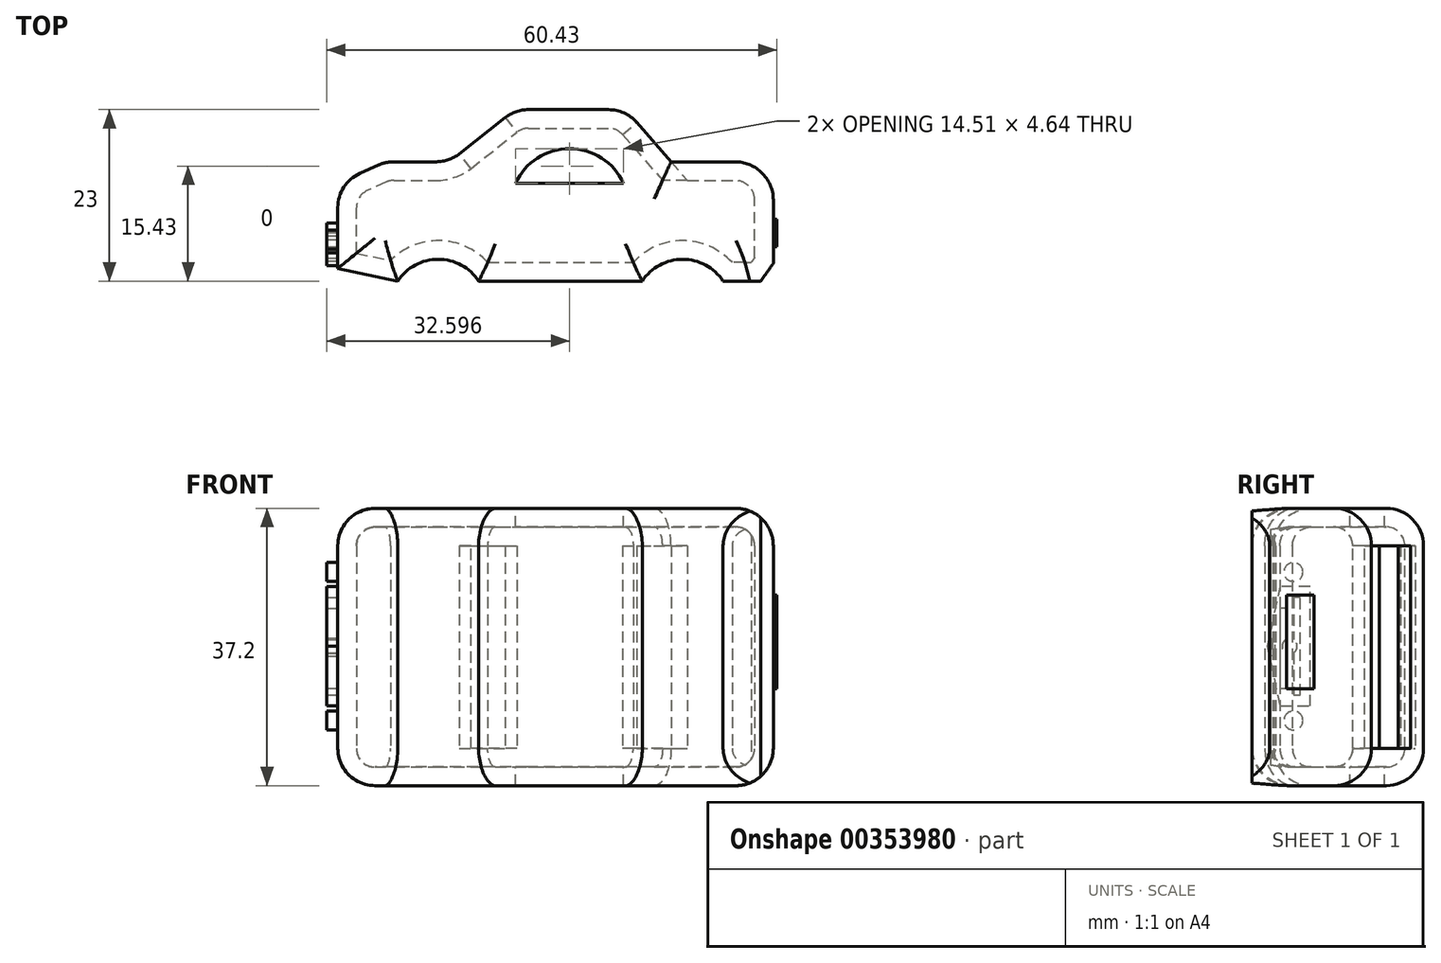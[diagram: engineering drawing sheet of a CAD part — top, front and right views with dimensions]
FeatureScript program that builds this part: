
annotation { "Feature Type Name" : "Feature", "Feature Type Description" : "" }
export const myFeature = defineFeature(function(context is Context, id is Id, definition is map)
    precondition{}
    {
        {
            var Q0;
            Q0=qCreatedBy(makeId("Top.planeOp"),FACE);
            var sketch = newSketch(context, id + "F0", { "sketchPlane" : qUnion([Q0])});
            skArc(sketch, "E0", {"start": v(-4.94, -13.11) * mm, "mid": v(-10.36, -10.2) * mm, "end": v(-15.79, -13.11) * mm});
            skArc(sketch, "E1", {"start": v(27.86, -13.11) * mm, "mid": v(22.43, -10.2) * mm, "end": v(17, -13.11) * mm});
            skLineSegment(sketch, "E2", {"start": v(-4.94, -13.11) * mm, "end": v(17, -13.11) * mm});
            skLineSegment(sketch, "E3", {"start": v(-15.79, -13.11) * mm, "end": v(-23.84, -11.41) * mm});
            skLineSegment(sketch, "E4", {"start": v(-23.84, -11.41) * mm, "end": v(-23.84, 0) * mm});
            skLineSegment(sketch, "E5", {"start": v(-23.84, 0) * mm, "end": v(-17.4, 2.9) * mm});
            skLineSegment(sketch, "E6", {"start": v(-17.4, 2.9) * mm, "end": v(-8.89, 2.9) * mm});
            skLineSegment(sketch, "E7", {"start": v(-8.89, 2.9) * mm, "end": v(0, 9.89) * mm});
            skLineSegment(sketch, "E8", {"start": v(0, 9.89) * mm, "end": v(14.75, 9.89) * mm});
            skLineSegment(sketch, "E9", {"start": v(14.75, 9.89) * mm, "end": v(20.87, 2.9) * mm});
            skLineSegment(sketch, "E10", {"start": v(20.87, 2.9) * mm, "end": v(31.44, 2.9) * mm});
            skLineSegment(sketch, "E11", {"start": v(27.86, -13.11) * mm, "end": v(32.92, -13.11) * mm});
            skLineSegment(sketch, "E12", {"start": v(34.59, -10.75) * mm, "end": v(34.59, 0) * mm});
            skLineSegment(sketch, "E13", {"start": v(31.44, 2.9) * mm, "end": v(34.59, 0) * mm});
            skPoint(sketch, "E14.start.orphan", {"position": v(34.59, 2.9) * mm});
            skLineSegment(sketch, "E15", {"start": v(34.59, -10.75) * mm, "end": v(32.92, -13.11) * mm});
            skPoint(sketch, "E16.orphan", {"position": v(34.59, -13.11) * mm});
            skSolve(sketch);
        }
        {
            var Q0;
            Q0 = qSketchRegion(id + "F0", true);
            extrude(context, id + "F1", {"entities" : qUnion([Q0]), "depth" : 37.2 * mm});
        }
        {
            var Q0;
            Q0=makeQuery(id+"F1.opExtrude","SWEPT_EDGE",EDGE,{"disambiguationData":[OSD([sQuery(id+"F0.wireOp",EDGE,"E5"),sQuery(id+"F0.wireOp",EDGE,"E6")])]});
            var Q1;
            Q1=makeQuery(id+"F1.opExtrude","SWEPT_EDGE",EDGE,{"disambiguationData":[OSD([sQuery(id+"F0.wireOp",EDGE,"E4"),sQuery(id+"F0.wireOp",EDGE,"E5")])]});
            var Q2;
            Q2=makeQuery(id+"F1.opExtrude","CAP_EDGE",EDGE,{"disambiguationData":[OSD([sQuery(id+"F0.wireOp",EDGE,"E5")])],"isStart":false});
            var Q3;
            Q3=makeQuery(id+"F1.opExtrude","CAP_EDGE",EDGE,{"disambiguationData":[OSD([sQuery(id+"F0.wireOp",EDGE,"E6")])],"isStart":false});
            var Q4;
            Q4=makeQuery(id+"F1.opExtrude","CAP_EDGE",EDGE,{"disambiguationData":[OSD([sQuery(id+"F0.wireOp",EDGE,"E7")])],"isStart":false});
            var Q5;
            Q5=makeQuery(id+"F1.opExtrude","CAP_EDGE",EDGE,{"disambiguationData":[OSD([sQuery(id+"F0.wireOp",EDGE,"E4")])],"isStart":false});
            var Q6;
            Q6=makeQuery(id+"F1.opExtrude","CAP_EDGE",EDGE,{"disambiguationData":[OSD([sQuery(id+"F0.wireOp",EDGE,"E3")])],"isStart":false});
            var Q7;
            Q7=makeQuery(id+"F1.opExtrude","CAP_EDGE",EDGE,{"disambiguationData":[OSD([sQuery(id+"F0.wireOp",EDGE,"E0")])],"isStart":false});
            var Q8;
            Q8=makeQuery(id+"F1.opExtrude","CAP_FACE",FACE,{"disambiguationData":[OSD([sQuery(id+"F0.wireOp",EDGE,"E0"),sQuery(id+"F0.wireOp",EDGE,"E1"),sQuery(id+"F0.wireOp",EDGE,"E2"),sQuery(id+"F0.wireOp",EDGE,"E3"),sQuery(id+"F0.wireOp",EDGE,"E4"),sQuery(id+"F0.wireOp",EDGE,"E5"),sQuery(id+"F0.wireOp",EDGE,"E6"),sQuery(id+"F0.wireOp",EDGE,"E7"),sQuery(id+"F0.wireOp",EDGE,"E8"),sQuery(id+"F0.wireOp",EDGE,"E9"),sQuery(id+"F0.wireOp",EDGE,"E10"),sQuery(id+"F0.wireOp",EDGE,"E11"),sQuery(id+"F0.wireOp",EDGE,"E12"),sQuery(id+"F0.wireOp",EDGE,"E13"),sQuery(id+"F0.wireOp",EDGE,"E15")])],"isStart":false});
            var Q9;
            Q9=makeQuery(id+"F1.opExtrude","CAP_EDGE",EDGE,{"disambiguationData":[OSD([sQuery(id+"F0.wireOp",EDGE,"E12")])],"isStart":true});
            var Q10;
            Q10=makeQuery(id+"F1.opExtrude","CAP_EDGE",EDGE,{"disambiguationData":[OSD([sQuery(id+"F0.wireOp",EDGE,"E10")])],"isStart":true});
            var Q11;
            Q11=makeQuery(id+"F1.opExtrude","CAP_EDGE",EDGE,{"disambiguationData":[OSD([sQuery(id+"F0.wireOp",EDGE,"E13")])],"isStart":true});
            var Q12;
            Q12=makeQuery(id+"F1.opExtrude","CAP_FACE",FACE,{"disambiguationData":[OSD([sQuery(id+"F0.wireOp",EDGE,"E0"),sQuery(id+"F0.wireOp",EDGE,"E1"),sQuery(id+"F0.wireOp",EDGE,"E2"),sQuery(id+"F0.wireOp",EDGE,"E3"),sQuery(id+"F0.wireOp",EDGE,"E4"),sQuery(id+"F0.wireOp",EDGE,"E5"),sQuery(id+"F0.wireOp",EDGE,"E6"),sQuery(id+"F0.wireOp",EDGE,"E7"),sQuery(id+"F0.wireOp",EDGE,"E8"),sQuery(id+"F0.wireOp",EDGE,"E9"),sQuery(id+"F0.wireOp",EDGE,"E10"),sQuery(id+"F0.wireOp",EDGE,"E11"),sQuery(id+"F0.wireOp",EDGE,"E12"),sQuery(id+"F0.wireOp",EDGE,"E13"),sQuery(id+"F0.wireOp",EDGE,"E15")])],"isStart":true});
            var Q13;
            Q13=makeQuery(id+"F1.opExtrude","SWEPT_EDGE",EDGE,{"disambiguationData":[OSD([sQuery(id+"F0.wireOp",EDGE,"E7"),sQuery(id+"F0.wireOp",EDGE,"E8")])]});
            var Q14;
            Q14=makeQuery(id+"F1.opExtrude","SWEPT_EDGE",EDGE,{"disambiguationData":[OSD([sQuery(id+"F0.wireOp",EDGE,"E8"),sQuery(id+"F0.wireOp",EDGE,"E9")])]});
            var Q15;
            Q15=makeQuery(id+"F1.opExtrude","SWEPT_EDGE",EDGE,{"disambiguationData":[OSD([sQuery(id+"F0.wireOp",EDGE,"E10"),sQuery(id+"F0.wireOp",EDGE,"E13")])]});
            var Q16;
            Q16=makeQuery(id+"F1.opExtrude","SWEPT_EDGE",EDGE,{"disambiguationData":[OSD([sQuery(id+"F0.wireOp",EDGE,"E12"),sQuery(id+"F0.wireOp",EDGE,"E13")])]});
            var Q17;
            Q17=makeQuery(id+"F1.opExtrude","SWEPT_EDGE",EDGE,{"disambiguationData":[OSD([sQuery(id+"F0.wireOp",EDGE,"E6"),sQuery(id+"F0.wireOp",EDGE,"E7")])]});
            fillet(context, id + "F2", {"entities" : qUnion([Q0, Q1, Q2, Q3, Q4, Q5, Q6, Q7, Q8, Q9, Q10, Q11, Q12, Q13, Q14, Q15, Q16, Q17]), "radius" : 5 * mm, "tangentPropagation" : true, "allowEdgeOverflow" : false});
        }
        {
            var Q0;
            Q0=makeQuery(id+"F1.opExtrude","SWEPT_FACE",FACE,{"disambiguationData":[OSD([sQuery(id+"F0.wireOp",EDGE,"E4")])]});
            var sketch = newSketch(context, id + "F3", { "sketchPlane" : qUnion([Q0])});
            skLineSegment(sketch, "E17", {"start": v(9.3, 10.7) * mm, "end": v(5.3, 10.7) * mm});
            skLineSegment(sketch, "E18", {"start": v(5.3, 10.7) * mm, "end": v(5.3, 26.7) * mm});
            skLineSegment(sketch, "E19", {"start": v(5.3, 26.7) * mm, "end": v(9.3, 26.7) * mm});
            skLineSegment(sketch, "E20", {"start": v(9.3, 10.7) * mm, "end": v(11.02, 18.7) * mm});
            skLineSegment(sketch, "E21", {"start": v(11.02, 18.7) * mm, "end": v(9.3, 26.7) * mm});
            skPoint(sketch, "E22.start.orphan", {"position": v(9.3, 18.7) * mm});
            skPoint(sketch, "E23.orphan", {"position": v(7.33, 5) * mm});
            skPoint(sketch, "E24.end.orphan", {"position": v(7.33, 32.2) * mm});
            skLineSegment(sketch, "E25", {"start": v(7.56, 12.14) * mm, "end": v(6.62, 12.14) * mm});
            skLineSegment(sketch, "E26", {"start": v(6.62, 12.14) * mm, "end": v(6.62, 25.27) * mm});
            skLineSegment(sketch, "E27", {"start": v(6.62, 25.27) * mm, "end": v(7.56, 25.27) * mm});
            skLineSegment(sketch, "E28", {"start": v(7.56, 25.27) * mm, "end": v(7.56, 19.57) * mm});
            skPoint(sketch, "E29.end.orphan", {"position": v(9.3, 21.98) * mm});
            skLineSegment(sketch, "E30", {"start": v(8.5, 13.08) * mm, "end": v(8.5, 17.8) * mm});
            skLineSegment(sketch, "E31", {"start": v(8.5, 23.8) * mm, "end": v(9.37, 23.8) * mm});
            skLineSegment(sketch, "E32", {"start": v(9.37, 23.8) * mm, "end": v(9.37, 13.08) * mm});
            skLineSegment(sketch, "E33", {"start": v(9.37, 13.08) * mm, "end": v(8.5, 13.08) * mm});
            skLineSegment(sketch, "E34", {"start": v(10.04, 17.4) * mm, "end": v(10.04, 19.8) * mm});
            skLineSegment(sketch, "E35", {"start": v(10.04, 19.8) * mm, "end": v(10.38, 19.8) * mm});
            skLineSegment(sketch, "E36", {"start": v(10.38, 19.8) * mm, "end": v(10.38, 17.4) * mm});
            skLineSegment(sketch, "E37", {"start": v(10.38, 17.4) * mm, "end": v(10.04, 17.4) * mm});
            skCircle(sketch, "E38", {"center": v(8.07, 18.7) * mm, "radius": 1 * mm});
            skLineSegment(sketch, "E39.trimOffspring", {"start": v(7.56, 17.83) * mm, "end": v(7.56, 12.14) * mm});
            skLineSegment(sketch, "E40.trimOffspring", {"start": v(8.5, 19.6) * mm, "end": v(8.5, 23.8) * mm});
            skCircle(sketch, "E41", {"center": v(7.56, 8.74) * mm, "radius": 1.27 * mm});
            skCircle(sketch, "E42", {"center": v(7.56, 28.66) * mm, "radius": 1.27 * mm});
            skSolve(sketch);
        }
        {
            var Q0;
            Q0 = qSketchRegion(id + "F3", true);
            var Q1;
            {var subQ0=sQuery(id+"F3.wireOp",EDGE,"E38");var subQ1=makeQuery(id+"F3.imprint","INTERSECT",VERTEX,{"derivedFrom":[sQuery(id+"F3.wireOp",EDGE,"E28"),subQ0]});Q1=makeQuery(id+"F3.imprint","IMPRINT",FACE,{"disambiguationData":[TD([[makeQuery(id+"F3.imprint","IMPRINT",EDGE,{"disambiguationData":[TD([[subQ1,1.0]])],"derivedFrom":subQ0}),1.0]])]});}
            extrude(context, id + "F4", {"entities" : qUnion([Q0, Q1]), "operationType" : NewBodyOperationType.ADD, "depth" : 1.5 * mm});
        }
        {
            var Q0;
            Q0=makeQuery(id+"F1.opExtrude","SWEPT_FACE",FACE,{"disambiguationData":[OSD([sQuery(id+"F0.wireOp",EDGE,"E12")])]});
            var sketch = newSketch(context, id + "F5", { "sketchPlane" : qUnion([Q0])});
            skLineSegment(sketch, "E43.bottom", {"start": v(-8.48, 25.54) * mm, "end": v(-4.81, 25.54) * mm});
            skLineSegment(sketch, "E43.top", {"start": v(-8.48, 12.99) * mm, "end": v(-4.81, 12.99) * mm});
            skLineSegment(sketch, "E43.left", {"start": v(-8.48, 25.54) * mm, "end": v(-8.48, 12.99) * mm});
            skLineSegment(sketch, "E43.right", {"start": v(-4.81, 25.54) * mm, "end": v(-4.81, 12.99) * mm});
            skPoint(sketch, "E43.middle", {"position": v(-6.65, 19.26) * mm});
            skSolve(sketch);
        }
        {
            var Q0;
            Q0 = qSketchRegion(id + "F5", true);
            extrude(context, id + "F6", {"entities" : qUnion([Q0]), "operationType" : NewBodyOperationType.ADD, "depth" : .5 * mm});
        }
        {
            var Q0;
            Q0=makeQuery(id+"F1.opExtrude","SWEPT_FACE",FACE,{"disambiguationData":[OSD([sQuery(id+"F0.wireOp",EDGE,"E7")])]});
            var Q1;
            Q1=makeQuery(id+"F1.opExtrude","SWEPT_FACE",FACE,{"disambiguationData":[OSD([sQuery(id+"F0.wireOp",EDGE,"E9")])]});
            shell(context, id + "F7", {"entities" : qUnion([Q0, Q1]), "thickness" : 2.5 * mm});
        }
        {
            var Q0;
            Q0=makeQuery(id+"F1.opExtrude","CAP_FACE",FACE,{"disambiguationData":[OSD([sQuery(id+"F0.wireOp",EDGE,"E0"),sQuery(id+"F0.wireOp",EDGE,"E1"),sQuery(id+"F0.wireOp",EDGE,"E2"),sQuery(id+"F0.wireOp",EDGE,"E3"),sQuery(id+"F0.wireOp",EDGE,"E4"),sQuery(id+"F0.wireOp",EDGE,"E5"),sQuery(id+"F0.wireOp",EDGE,"E6"),sQuery(id+"F0.wireOp",EDGE,"E7"),sQuery(id+"F0.wireOp",EDGE,"E8"),sQuery(id+"F0.wireOp",EDGE,"E9"),sQuery(id+"F0.wireOp",EDGE,"E10"),sQuery(id+"F0.wireOp",EDGE,"E11"),sQuery(id+"F0.wireOp",EDGE,"E12"),sQuery(id+"F0.wireOp",EDGE,"E13"),sQuery(id+"F0.wireOp",EDGE,"E15")])],"isStart":false});
            var sketch = newSketch(context, id + "F8", { "sketchPlane" : qUnion([Q0])});
            skArc(sketch, "E44", {"start": v(14.51, 0) * mm, "mid": v(7.26, 4.64) * mm, "end": v(0, 0) * mm});
            skLineSegment(sketch, "E45", {"start": v(0, 0) * mm, "end": v(14.51, 0) * mm});
            skSolve(sketch);
        }
        {
            var Q0;
            Q0 = qSketchRegion(id + "F8", true);
            extrude(context, id + "F9", {"entities" : qUnion([Q0]), "operationType" : NewBodyOperationType.REMOVE, "endBound" : BoundingType.SYMMETRIC, "oppositeDirection" : true, "depth" : 103.4 * mm});
        }
    });
